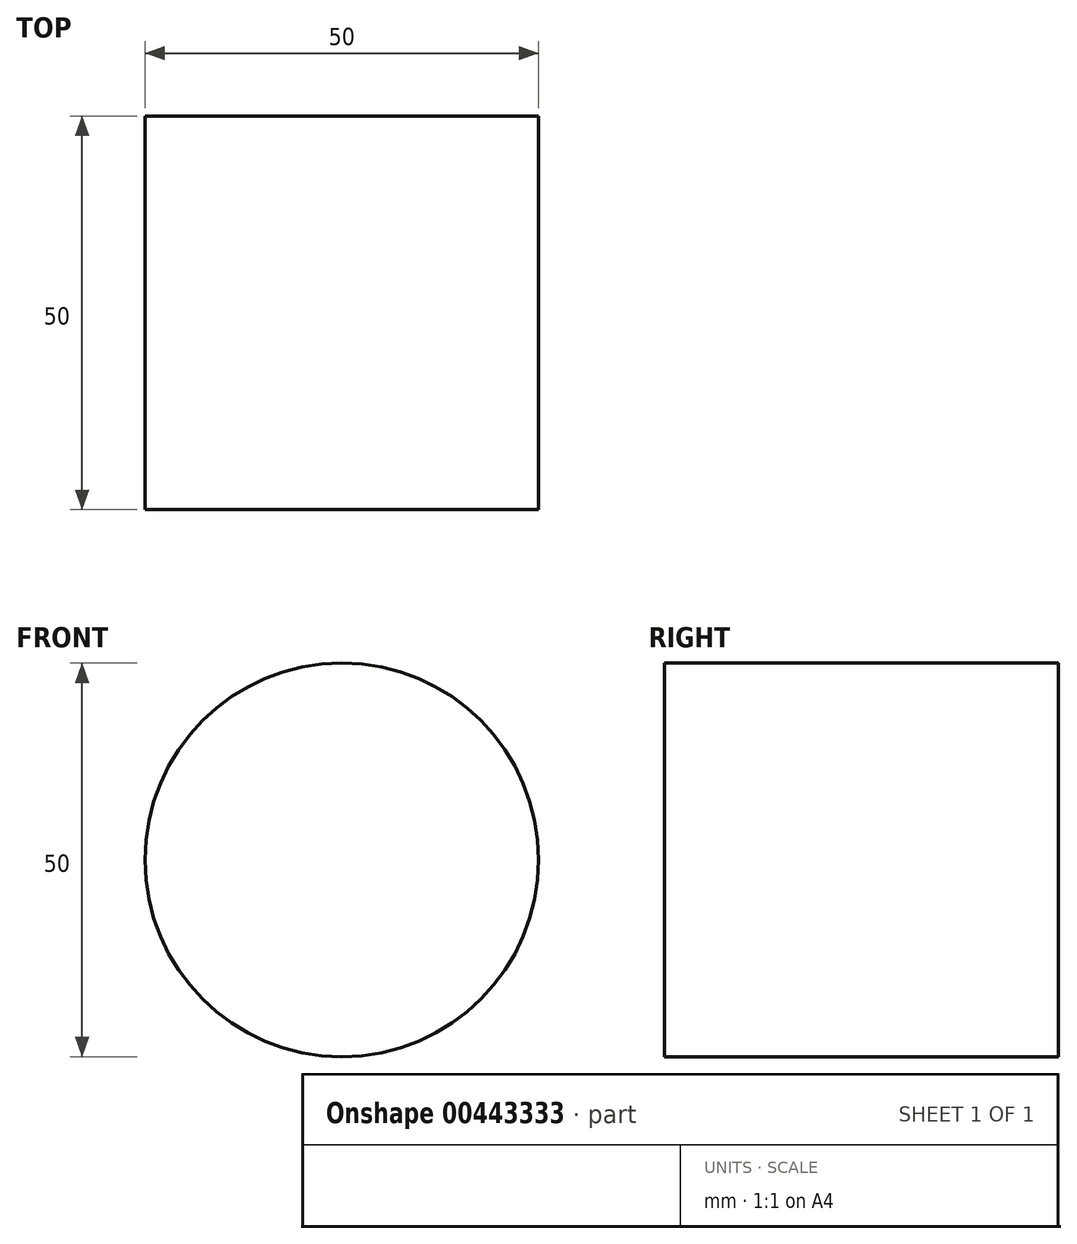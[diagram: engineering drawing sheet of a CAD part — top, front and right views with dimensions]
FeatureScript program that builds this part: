
annotation { "Feature Type Name" : "Feature", "Feature Type Description" : "" }
export const myFeature = defineFeature(function(context is Context, id is Id, definition is map)
    precondition{}
    {
        {
            var Q0;
            Q0=qCreatedBy(makeId("Front.planeOp"),FACE);
            var sketch = newSketch(context, id + "F0", { "sketchPlane" : qUnion([Q0])});
            skCircle(sketch, "E0", {"center": v(0, 0) * mm, "radius": 25 * mm});
            skSolve(sketch);
        }
        {
            var Q0;
            Q0=makeQuery(id+"F0.imprint","IMPRINT",FACE,{"disambiguationData":[TD([[makeQuery(id+"F0.imprint","IMPRINT",EDGE,{"derivedFrom":sQuery(id+"F0.wireOp",EDGE,"E0")}),1.0]])]});
            extrude(context, id + "F1", {"entities" : qUnion([Q0]), "depth" : 50 * mm, "symmetric" : true});
        }
    });
